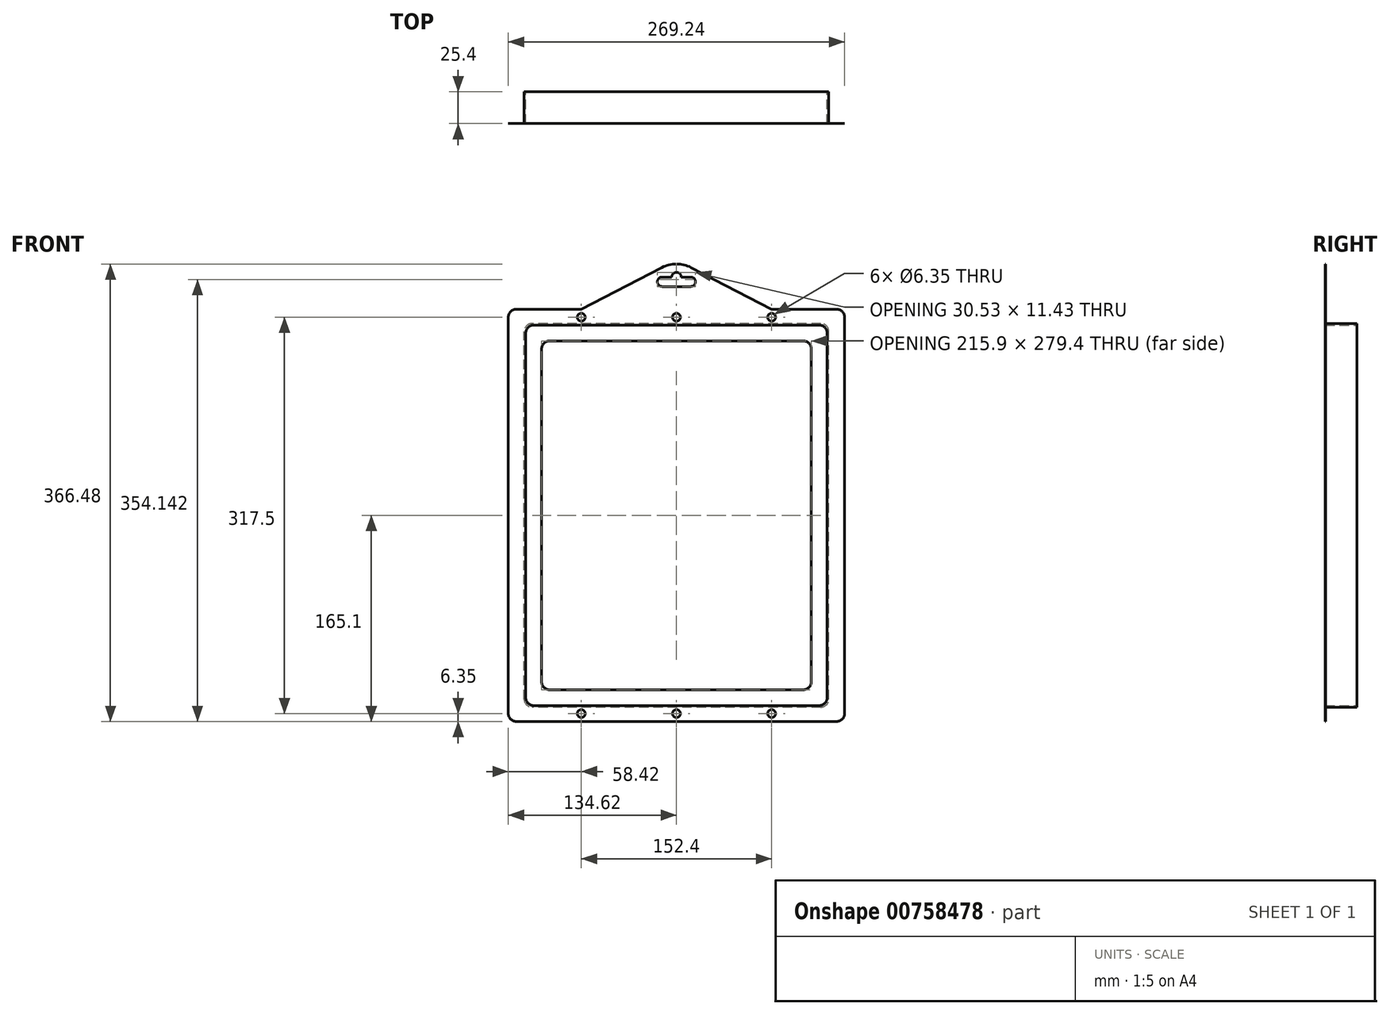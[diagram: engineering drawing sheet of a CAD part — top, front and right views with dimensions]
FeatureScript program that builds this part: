
annotation { "Feature Type Name" : "Feature", "Feature Type Description" : "" }
export const myFeature = defineFeature(function(context is Context, id is Id, definition is map)
    precondition{}
    {
        {
            var Q0;
            Q0=qCreatedBy(makeId("Front.planeOp"),FACE);
            var sketch = newSketch(context, id + "F0", { "sketchPlane" : qUnion([Q0])});
            skLineSegment(sketch, "E0.bottom", {"start": v(101.6, -139.7) * mm, "end": v(-101.6, -139.7) * mm});
            skLineSegment(sketch, "E0.top", {"start": v(101.6, 139.7) * mm, "end": v(-101.6, 139.7) * mm});
            skLineSegment(sketch, "E0.left", {"start": v(107.95, -133.35) * mm, "end": v(107.95, 133.35) * mm});
            skLineSegment(sketch, "E0.right", {"start": v(-107.95, -133.35) * mm, "end": v(-107.95, 133.35) * mm});
            skPoint(sketch, "E0.middle", {"position": v(0, 0) * mm});
            skLineSegment(sketch, "E1.bottom", {"start": v(114.3, -152.4) * mm, "end": v(-114.3, -152.4) * mm});
            skLineSegment(sketch, "E1.top", {"start": v(114.3, 152.4) * mm, "end": v(-114.3, 152.4) * mm});
            skLineSegment(sketch, "E1.left", {"start": v(120.65, -146.05) * mm, "end": v(120.65, 146.05) * mm});
            skLineSegment(sketch, "E1.right", {"start": v(-120.65, -146.05) * mm, "end": v(-120.65, 146.05) * mm});
            skPoint(sketch, "E2.visualSharp", {"position": v(-120.65, 152.4) * mm});
            skArc(sketch, "E2.filletArc", {"start": v(-114.3, 152.4) * mm, "mid": v(-118.8, 150.54) * mm, "end": v(-120.65, 146.05) * mm});
            skPoint(sketch, "E3.visualSharp", {"position": v(120.65, 152.4) * mm});
            skArc(sketch, "E3.filletArc", {"start": v(120.65, 146.05) * mm, "mid": v(118.8, 150.54) * mm, "end": v(114.3, 152.4) * mm});
            skPoint(sketch, "E4.visualSharp", {"position": v(120.65, -152.4) * mm});
            skArc(sketch, "E4.filletArc", {"start": v(114.3, -152.4) * mm, "mid": v(118.8, -150.54) * mm, "end": v(120.65, -146.05) * mm});
            skPoint(sketch, "E5.visualSharp", {"position": v(-120.65, -152.4) * mm});
            skArc(sketch, "E5.filletArc", {"start": v(-120.65, -146.05) * mm, "mid": v(-118.8, -150.54) * mm, "end": v(-114.3, -152.4) * mm});
            skPoint(sketch, "E6.visualSharp", {"position": v(-107.95, -139.7) * mm});
            skArc(sketch, "E6.filletArc", {"start": v(-107.95, -133.35) * mm, "mid": v(-106.1, -137.84) * mm, "end": v(-101.6, -139.7) * mm});
            skPoint(sketch, "E7.visualSharp", {"position": v(107.95, -139.7) * mm});
            skArc(sketch, "E7.filletArc", {"start": v(101.6, -139.7) * mm, "mid": v(106.1, -137.84) * mm, "end": v(107.95, -133.35) * mm});
            skPoint(sketch, "E8.visualSharp", {"position": v(107.95, 139.7) * mm});
            skArc(sketch, "E8.filletArc", {"start": v(107.95, 133.35) * mm, "mid": v(106.1, 137.84) * mm, "end": v(101.6, 139.7) * mm});
            skPoint(sketch, "E9.visualSharp", {"position": v(-107.95, 139.7) * mm});
            skArc(sketch, "E9.filletArc", {"start": v(-101.6, 139.7) * mm, "mid": v(-106.1, 137.84) * mm, "end": v(-107.95, 133.35) * mm});
            skLineSegment(sketch, "E10.bottom", {"start": v(115.57, -153.67) * mm, "end": v(-115.57, -153.67) * mm});
            skLineSegment(sketch, "E10.top", {"start": v(115.57, 153.67) * mm, "end": v(-115.57, 153.67) * mm});
            skLineSegment(sketch, "E10.left", {"start": v(121.92, -147.32) * mm, "end": v(121.92, 147.32) * mm});
            skLineSegment(sketch, "E10.right", {"start": v(-121.92, -147.32) * mm, "end": v(-121.92, 147.32) * mm});
            skPoint(sketch, "E11.visualSharp", {"position": v(-121.92, -153.67) * mm});
            skArc(sketch, "E11.filletArc", {"start": v(-121.92, -147.32) * mm, "mid": v(-120.06, -151.81) * mm, "end": v(-115.57, -153.67) * mm});
            skPoint(sketch, "E12.visualSharp", {"position": v(121.92, -153.67) * mm});
            skArc(sketch, "E12.filletArc", {"start": v(115.57, -153.67) * mm, "mid": v(120.06, -151.81) * mm, "end": v(121.92, -147.32) * mm});
            skPoint(sketch, "E13.visualSharp", {"position": v(121.92, 153.67) * mm});
            skArc(sketch, "E13.filletArc", {"start": v(121.92, 147.32) * mm, "mid": v(120.06, 151.81) * mm, "end": v(115.57, 153.67) * mm});
            skPoint(sketch, "E14.visualSharp", {"position": v(-121.92, 153.67) * mm});
            skArc(sketch, "E14.filletArc", {"start": v(-115.57, 153.67) * mm, "mid": v(-120.06, 151.81) * mm, "end": v(-121.92, 147.32) * mm});
            skPoint(sketch, "E15.visualSharp", {"position": v(-134.62, 165.1) * mm});
            skPoint(sketch, "E16.visualSharp", {"position": v(134.62, 165.1) * mm});
            skPoint(sketch, "E17.visualSharp", {"position": v(-134.62, -165.1) * mm});
            skSolve(sketch);
        }
        {
            var Q0;
            Q0=makeQuery(id+"F0.imprint","IMPRINT",FACE,{"disambiguationData":[TD([[makeQuery(id+"F0.imprint","IMPRINT",EDGE,{"derivedFrom":sQuery(id+"F0.wireOp",EDGE,"E1.bottom")}),1.0]])]});
            extrude(context, id + "F1", {"entities" : qUnion([Q0]), "depth" : 25.4 * mm, "offsetDistance" : 25.4 * mm});
        }
        {
            var Q0;
            Q0=makeQuery(id+"F0.imprint","IMPRINT",FACE,{"disambiguationData":[TD([[makeQuery(id+"F0.imprint","IMPRINT",EDGE,{"derivedFrom":sQuery(id+"F0.wireOp",EDGE,"E0.bottom")}),1.0]])]});
            extrude(context, id + "F2", {"entities" : qUnion([Q0]), "operationType" : NewBodyOperationType.ADD, "depth" : 0.25 * mm, "offsetDistance" : 25.4 * mm});
        }
        {
            var Q0;
            Q0=makeQuery(id+"F1.opExtrude","CAP_FACE",FACE,{"disambiguationData":[OSD([sQuery(id+"F0.wireOp",EDGE,"E1.bottom"),sQuery(id+"F0.wireOp",EDGE,"E1.top"),sQuery(id+"F0.wireOp",EDGE,"E1.left"),sQuery(id+"F0.wireOp",EDGE,"E1.right"),sQuery(id+"F0.wireOp",EDGE,"E2.filletArc"),sQuery(id+"F0.wireOp",EDGE,"E3.filletArc"),sQuery(id+"F0.wireOp",EDGE,"E4.filletArc"),sQuery(id+"F0.wireOp",EDGE,"E5.filletArc"),sQuery(id+"F0.wireOp",EDGE,"E10.bottom"),sQuery(id+"F0.wireOp",EDGE,"E10.top"),sQuery(id+"F0.wireOp",EDGE,"E10.left"),sQuery(id+"F0.wireOp",EDGE,"E10.right"),sQuery(id+"F0.wireOp",EDGE,"E11.filletArc"),sQuery(id+"F0.wireOp",EDGE,"E12.filletArc"),sQuery(id+"F0.wireOp",EDGE,"E13.filletArc"),sQuery(id+"F0.wireOp",EDGE,"E14.filletArc")])],"isStart":false});
            var sketch = newSketch(context, id + "F3", { "sketchPlane" : qUnion([Q0])});
            skLineSegment(sketch, "E18.bottom", {"start": v(128.27, -165.1) * mm, "end": v(-128.27, -165.1) * mm});
            skLineSegment(sketch, "E18.top", {"start": v(128.27, 165.1) * mm, "end": v(76.2, 165.1) * mm});
            skLineSegment(sketch, "E18.left", {"start": v(134.62, -158.75) * mm, "end": v(134.62, 158.75) * mm});
            skLineSegment(sketch, "E18.right", {"start": v(-134.62, -158.75) * mm, "end": v(-134.62, 158.75) * mm});
            skPoint(sketch, "E18.middle", {"position": v(0, 0) * mm});
            skPoint(sketch, "E19.visualSharp", {"position": v(-134.62, 165.1) * mm});
            skArc(sketch, "E19.filletArc", {"start": v(-128.27, 165.1) * mm, "mid": v(-132.76, 163.24) * mm, "end": v(-134.62, 158.75) * mm});
            skPoint(sketch, "E20.visualSharp", {"position": v(134.62, 165.1) * mm});
            skArc(sketch, "E20.filletArc", {"start": v(134.62, 158.75) * mm, "mid": v(132.76, 163.24) * mm, "end": v(128.27, 165.1) * mm});
            skPoint(sketch, "E21.visualSharp", {"position": v(134.62, -165.1) * mm});
            skArc(sketch, "E21.filletArc", {"start": v(128.27, -165.1) * mm, "mid": v(132.76, -163.24) * mm, "end": v(134.62, -158.75) * mm});
            skPoint(sketch, "E22.visualSharp", {"position": v(-134.62, -165.1) * mm});
            skArc(sketch, "E22.filletArc", {"start": v(-134.62, -158.75) * mm, "mid": v(-132.76, -163.24) * mm, "end": v(-128.27, -165.1) * mm});
            skPoint(sketch, "E23.centerSnap0", {"position": v(134.62, 0) * mm});
            skPoint(sketch, "E24.centerSnap0", {"position": v(-120.65, 0) * mm});
            skLineSegment(sketch, "E25", {"start": v(-76.2, 165.1) * mm, "end": v(-11.69, 198.54) * mm});
            skLineSegment(sketch, "E26", {"start": v(11.69, 198.54) * mm, "end": v(76.2, 165.1) * mm});
            skPoint(sketch, "E27.visualSharp", {"position": v(0, 204.6) * mm});
            skArc(sketch, "E27.filletArc", {"start": v(11.69, 198.54) * mm, "mid": v(0, 201.38) * mm, "end": v(-11.69, 198.54) * mm});
            skLineSegment(sketch, "E28.trimOffspring", {"start": v(-76.2, 165.1) * mm, "end": v(-128.27, 165.1) * mm});
            skCircle(sketch, "E29", {"center": v(0, 190.95) * mm, "radius": 3.81 * mm});
            skLineSegment(sketch, "E30.bottom", {"start": v(11.45, 190.95) * mm, "end": v(-11.45, 190.95) * mm});
            skLineSegment(sketch, "E30.top", {"start": v(11.45, 183.33) * mm, "end": v(-11.45, 183.33) * mm});
            skLineSegment(sketch, "E30.left", {"start": v(11.45, 190.95) * mm, "end": v(11.45, 183.33) * mm});
            skLineSegment(sketch, "E30.right", {"start": v(-11.45, 190.95) * mm, "end": v(-11.45, 183.33) * mm});
            skPoint(sketch, "E30.middle", {"position": v(0, 187.14) * mm});
            skCircle(sketch, "E31", {"center": v(11.45, 187.14) * mm, "radius": 3.8 * mm});
            skCircle(sketch, "E32", {"center": v(-11.45, 187.14) * mm, "radius": 3.8 * mm});
            skCircle(sketch, "E33", {"center": v(76.2, 158.75) * mm, "radius": 3.18 * mm});
            skCircle(sketch, "E34", {"center": v(-76.2, 158.75) * mm, "radius": 3.18 * mm});
            skCircle(sketch, "E35", {"center": v(0, 158.75) * mm, "radius": 3.18 * mm});
            skCircle(sketch, "E36", {"center": v(0, -158.75) * mm, "radius": 3.18 * mm});
            skPoint(sketch, "E36.centerSnap0", {"position": v(0, -153.67) * mm});
            skCircle(sketch, "E37", {"center": v(-76.2, -158.75) * mm, "radius": 3.18 * mm});
            skCircle(sketch, "E38", {"center": v(76.2, -158.75) * mm, "radius": 3.18 * mm});
            skSolve(sketch);
        }
        {
            var Q0;
            Q0=makeQuery(id+"F3.imprint","IMPRINT",FACE,{"disambiguationData":[TD([[makeQuery(id+"F3.imprint","IMPRINT",EDGE,{"derivedFrom":makeQuery(id+"F1.opExtrude","CAP_EDGE",EDGE,{"disambiguationData":[OSD([sQuery(id+"F0.wireOp",EDGE,"E1.bottom")])],"isStart":false})}),1.0]])]});
            var Q1;
            Q1=makeQuery(id+"F3.imprint","IMPRINT",FACE,{"disambiguationData":[TD([[makeQuery(id+"F3.imprint","IMPRINT",EDGE,{"derivedFrom":sQuery(id+"F3.wireOp",EDGE,"E18.bottom")}),-1.0]])]});
            extrude(context, id + "F4", {"entities" : qUnion([Q0, Q1]), "operationType" : NewBodyOperationType.ADD, "oppositeDirection" : true, "depth" : 0.25 * mm, "offsetDistance" : 25.4 * mm});
        }
    });
